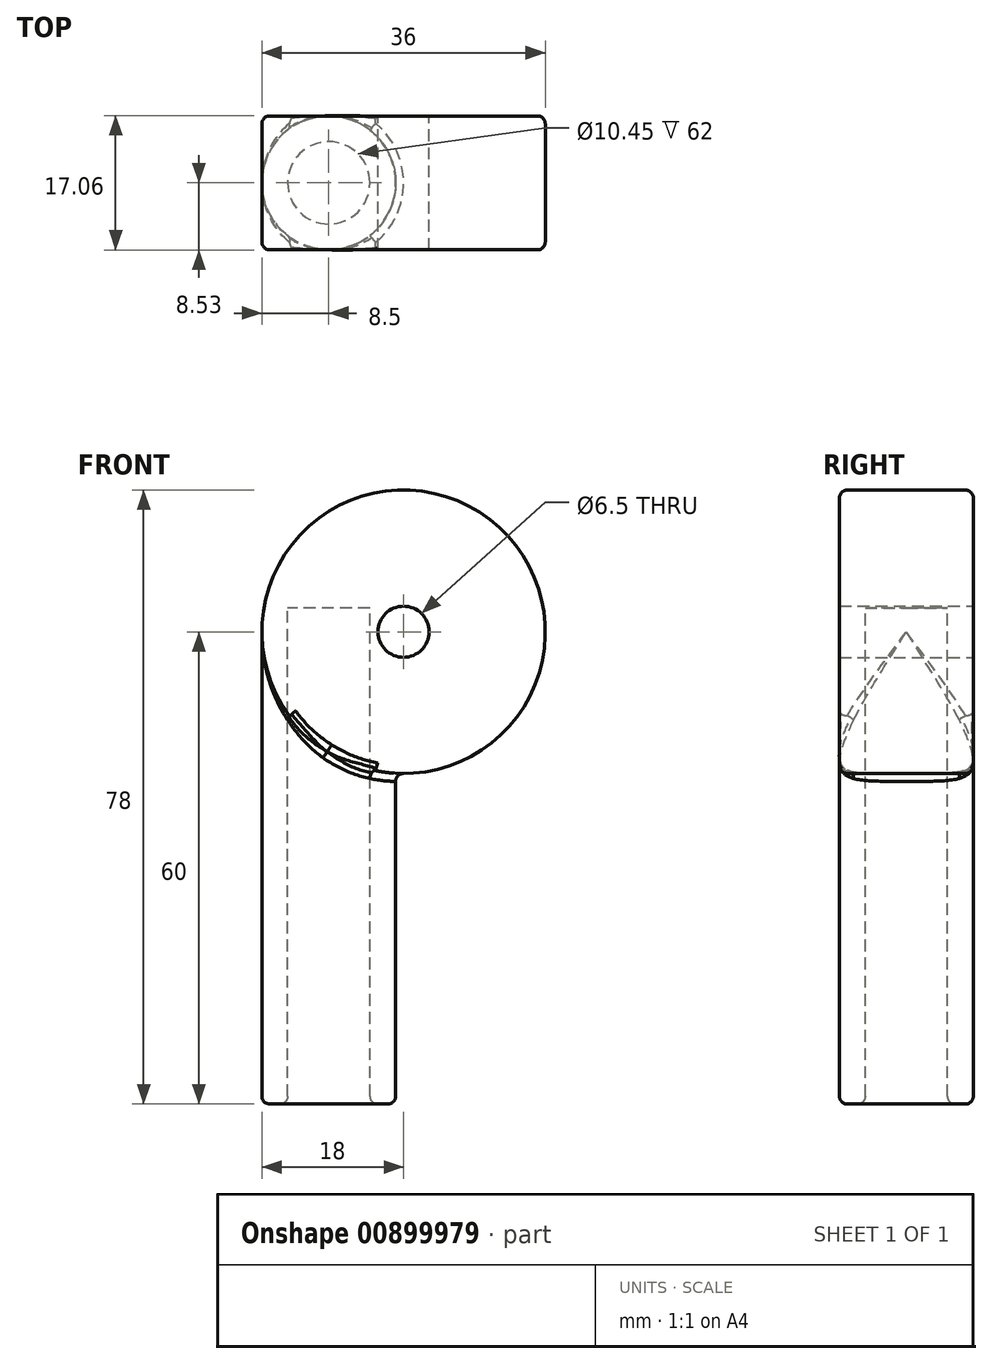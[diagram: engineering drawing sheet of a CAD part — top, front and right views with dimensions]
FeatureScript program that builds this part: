
annotation { "Feature Type Name" : "Feature", "Feature Type Description" : "" }
export const myFeature = defineFeature(function(context is Context, id is Id, definition is map)
    precondition{}
    {
        {
            assignVariable(context, id + "F0", {"name" : "longueur", "anyValue" : 60});
        }
        {
            var Q0;
            Q0=qCreatedBy(makeId("Front.planeOp"),FACE);
            var sketch = newSketch(context, id + "F1", { "sketchPlane" : qUnion([Q0])});
            skCircle(sketch, "E0", {"center": v(0, 0) * mm, "radius": 18 * mm});
            skCircle(sketch, "E1", {"center": v(0, 0) * mm, "radius": 3.25 * mm});
            skSolve(sketch);
        }
        {
            var Q0;
            Q0=qSketchRegion(id+"F1",true);
            extrude(context, id + "F2", {"entities" : qUnion([Q0]), "depth" : 7.5 * mm, "offsetDistance" : 25 * mm, "hasSecondDirection" : true, "secondDirectionOppositeDirection" : true, "secondDirectionDepth" : 9.5 * mm});
        }
        {
            var Q0;
            Q0=qCreatedBy(makeId("Top.planeOp"),FACE);
            var sketch = newSketch(context, id + "F3", { "sketchPlane" : qUnion([Q0])});
            skCircle(sketch, "E2", {"center": v(-9.5, 1) * mm, "radius": 5.22 * mm});
            skCircle(sketch, "E3", {"center": v(-9.5, 1) * mm, "radius": 8.5 * mm});
            skLineSegment(sketch, "E4", {"start": v(-18, -7.5) * mm, "end": v(-18, 9.5) * mm, "construction": true});
            skSolve(sketch);
        }
        {
            var Q0;
            Q0=qSketchRegion(id+"F3",true);
            var Q1;
            Q1=makeQuery(id+"F3.imprint","IMPRINT",FACE,{"disambiguationData":[TD([[makeQuery(id+"F3.imprint","IMPRINT",EDGE,{"derivedFrom":sQuery(id+"F3.wireOp",EDGE,"E2")}),1.0]])]});
            extrude(context, id + "F4", {"entities" : qUnion([Q0, Q1]), "operationType" : NewBodyOperationType.ADD, "oppositeDirection" : true, "depth" : (getVariable(context, 'longueur')) * mm, "offsetDistance" : 25 * mm});
        }
        {
            var Q0;
            Q0=makeQuery(id+"F3.imprint","IMPRINT",FACE,{"disambiguationData":[TD([[makeQuery(id+"F3.imprint","IMPRINT",EDGE,{"derivedFrom":sQuery(id+"F3.wireOp",EDGE,"E2")}),1.0]])]});
            extrude(context, id + "F5", {"entities" : qUnion([Q0]), "operationType" : NewBodyOperationType.REMOVE, "endBound" : BoundingType.THROUGH_ALL, "oppositeDirection" : true, "depth" : 25 * mm, "offsetDistance" : 25 * mm, "hasSecondDirection" : true, "secondDirectionOppositeDirection" : false, "secondDirectionDepth" : 3 * mm});
        }
        {
            var Q0;
            Q0=makeQuery(id+"F1.imprint","IMPRINT",FACE,{"disambiguationData":[TD([[makeQuery(id+"F1.imprint","IMPRINT",EDGE,{"derivedFrom":sQuery(id+"F1.wireOp",EDGE,"E1")}),1.0]])]});
            extrude(context, id + "F6", {"entities" : qUnion([Q0]), "operationType" : NewBodyOperationType.REMOVE, "endBound" : BoundingType.THROUGH_ALL, "depth" : 25 * mm, "offsetDistance" : 25 * mm, "hasSecondDirection" : true, "secondDirectionBound" : SecondDirectionBoundingType.THROUGH_ALL, "secondDirectionOppositeDirection" : true, "secondDirectionDepth" : 25 * mm});
        }
        {
            var Q0;
            Q0=makeQuery(id+"F2.opExtrude","CAP_FACE",FACE,{"disambiguationData":[OSD([sQuery(id+"F1.wireOp",EDGE,"E0"),sQuery(id+"F1.wireOp",EDGE,"E1")])],"isStart":true});
            var sketch = newSketch(context, id + "F7", { "sketchPlane" : qUnion([Q0])});
            skCircle(sketch, "E5.cCircle", {"center": v(0, 0) * mm, "radius": 6.06 * mm, "construction": true});
            skLineSegment(sketch, "E5.0", {"start": v(3.03, 5.25) * mm, "end": v(6.06, 0) * mm});
            skLineSegment(sketch, "E5.2", {"start": v(3.03, -5.25) * mm, "end": v(-3.03, -5.25) * mm});
            skLineSegment(sketch, "E5.3", {"start": v(-3.03, -5.25) * mm, "end": v(-6.06, 0) * mm});
            skLineSegment(sketch, "E5.4", {"start": v(-6.06, 0) * mm, "end": v(-3.03, 5.25) * mm});
            skLineSegment(sketch, "E5.5", {"start": v(-3.03, 5.25) * mm, "end": v(3.03, 5.25) * mm});
            skLineSegment(sketch, "E6", {"start": v(6.06, 0) * mm, "end": v(3.03, -5.25) * mm});
            skSolve(sketch);
        }
        {
            var Q0;
            Q0=makeQuery(id+"F1.imprint","IMPRINT",FACE,{"disambiguationData":[TD([[makeQuery(id+"F1.imprint","IMPRINT",EDGE,{"derivedFrom":sQuery(id+"F1.wireOp",EDGE,"E1")}),1.0]])]});
            extrude(context, id + "F8", {"entities" : qUnion([Q0]), "operationType" : NewBodyOperationType.REMOVE, "endBound" : BoundingType.SYMMETRIC, "oppositeDirection" : true, "depth" : 100 * mm, "offsetDistance" : 25 * mm});
        }
        {
            var Q0;
            Q0=makeQuery(id+"F2.opExtrude","CAP_EDGE",EDGE,{"disambiguationData":[OSD([sQuery(id+"F1.wireOp",EDGE,"E0")])],"isStart":true});
            var Q1;
            Q1=makeQuery(id+"F4.boolean.opBoolean","INTERSECT",EDGE,{"disambiguationData":[OD(2.0)],"derivedFrom":[makeQuery(id+"F2.opExtrude","SWEPT_FACE",FACE,{"disambiguationData":[OSD([sQuery(id+"F1.wireOp",EDGE,"E0")])]}),makeQuery(id+"F4.opExtrude","SWEPT_FACE",FACE,{"disambiguationData":[OSD([sQuery(id+"F3.wireOp",EDGE,"E3")])]})]});
            var Q2;
            Q2=makeQuery(id+"F4.boolean.opBoolean","INTERSECT",EDGE,{"disambiguationData":[OD(0.0)],"derivedFrom":[makeQuery(id+"F2.opExtrude","SWEPT_FACE",FACE,{"disambiguationData":[OSD([sQuery(id+"F1.wireOp",EDGE,"E0")])]}),makeQuery(id+"F4.opExtrude","SWEPT_FACE",FACE,{"disambiguationData":[OSD([sQuery(id+"F3.wireOp",EDGE,"E3")])]})]});
            var Q3;
            Q3=makeQuery(id+"F4.boolean.opBoolean","INTERSECT",EDGE,{"disambiguationData":[OD(1.0)],"derivedFrom":[makeQuery(id+"F2.opExtrude","SWEPT_FACE",FACE,{"disambiguationData":[OSD([sQuery(id+"F1.wireOp",EDGE,"E0")])]}),makeQuery(id+"F4.opExtrude","SWEPT_FACE",FACE,{"disambiguationData":[OSD([sQuery(id+"F3.wireOp",EDGE,"E3")])]})]});
            var Q4;
            Q4=makeQuery(id+"F4.opExtrude","CAP_FACE",FACE,{"disambiguationData":[OSD([sQuery(id+"F3.wireOp",EDGE,"E3")])],"isStart":false});
            var Q5;
            Q5=makeQuery(id+"F2.opExtrude","CAP_EDGE",EDGE,{"disambiguationData":[OSD([sQuery(id+"F1.wireOp",EDGE,"E0")])],"isStart":false});
            fillet(context, id + "F9", {"entities" : qUnion([Q0, Q1, Q2, Q3, Q4, Q5]), "radius" : 1 * mm, "tangentPropagation" : true, "allowEdgeOverflow" : false});
        }
    });
